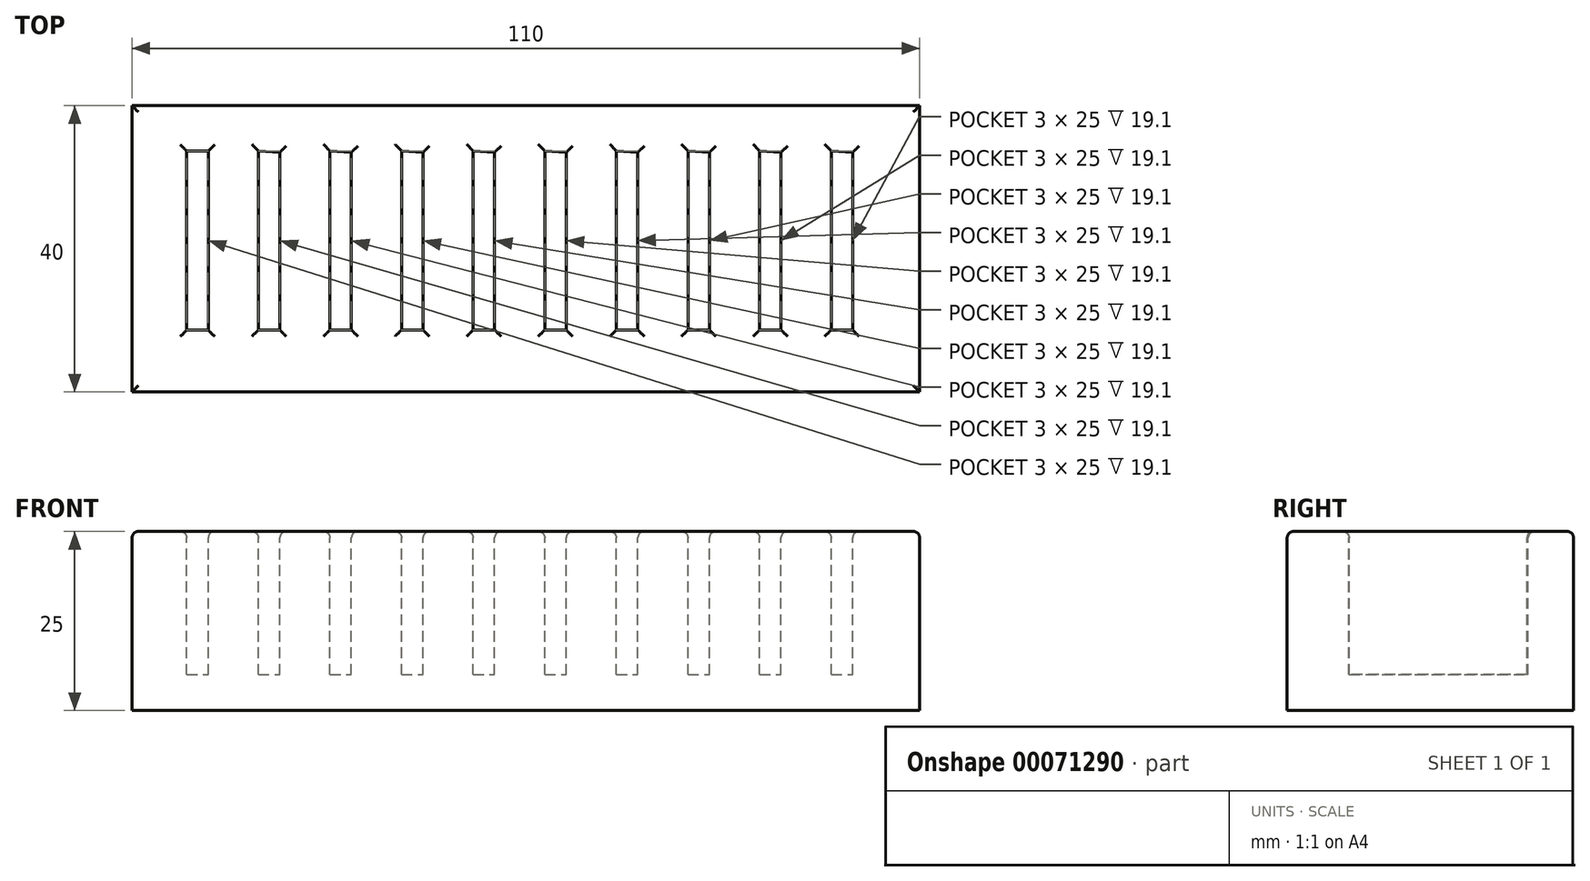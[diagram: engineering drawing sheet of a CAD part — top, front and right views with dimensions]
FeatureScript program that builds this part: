
annotation { "Feature Type Name" : "Feature", "Feature Type Description" : "" }
export const myFeature = defineFeature(function(context is Context, id is Id, definition is map)
    precondition{}
    {
        {
            var Q0;
            Q0=qCreatedBy(makeId("Top.planeOp"),FACE);
            var sketch = newSketch(context, id + "F0", { "sketchPlane" : qUnion([Q0])});
            skLineSegment(sketch, "E0.bottom", {"start": v(-54.52, 23.52) * mm, "end": v(55.48, 23.52) * mm});
            skLineSegment(sketch, "E0.top", {"start": v(-54.52, -16.48) * mm, "end": v(55.48, -16.48) * mm});
            skLineSegment(sketch, "E0.left", {"start": v(-54.52, 23.52) * mm, "end": v(-54.52, -16.48) * mm});
            skLineSegment(sketch, "E0.right", {"start": v(55.48, 23.52) * mm, "end": v(55.48, -16.48) * mm});
            skSolve(sketch);
        }
        {
            var Q0;
            Q0=makeQuery(id+"F0.imprint","IMPRINT",FACE,{"disambiguationData":[TD([[makeQuery(id+"F0.imprint","IMPRINT",EDGE,{"derivedFrom":sQuery(id+"F0.wireOp",EDGE,"E0.bottom")}),-1.0]])]});
            extrude(context, id + "F1", {"entities" : qUnion([Q0]), "depth" : 25 * mm});
        }
        {
            var Q0;
            Q0=makeQuery(id+"F1.opExtrude","CAP_FACE",FACE,{"disambiguationData":[OSD([sQuery(id+"F0.wireOp",EDGE,"E0.bottom"),sQuery(id+"F0.wireOp",EDGE,"E0.top"),sQuery(id+"F0.wireOp",EDGE,"E0.left"),sQuery(id+"F0.wireOp",EDGE,"E0.right")])],"isStart":false});
            var sketch = newSketch(context, id + "F2", { "sketchPlane" : qUnion([Q0])});
            skLineSegment(sketch, "E1.bottom", {"start": v(-46.88, -7.85) * mm, "end": v(-43.88, -7.85) * mm});
            skLineSegment(sketch, "E1.top", {"start": v(-46.88, 17.15) * mm, "end": v(-43.88, 17.15) * mm});
            skLineSegment(sketch, "E1.left", {"start": v(-46.88, -7.85) * mm, "end": v(-46.88, 17.15) * mm});
            skLineSegment(sketch, "E1.right", {"start": v(-43.88, -7.85) * mm, "end": v(-43.88, 17.15) * mm});
            skLineSegment(sketch, "E2", {"start": v(-43.88, -7.85) * mm, "end": v(-41.88, -7.83) * mm});
            skLineSegment(sketch, "E3.0", {"start": v(-36.88, -7.83) * mm, "end": v(-36.88, 17.17) * mm});
            skLineSegment(sketch, "E4", {"start": v(-36.88, -7.83) * mm, "end": v(-33.88, -7.83) * mm});
            skLineSegment(sketch, "E5", {"start": v(-33.88, 17.02) * mm, "end": v(-36.88, 17.17) * mm});
            skLineSegment(sketch, "E6", {"start": v(-33.88, 17.02) * mm, "end": v(-33.88, -7.83) * mm});
            skLineSegment(sketch, "E7.0", {"start": v(-26.88, -7.83) * mm, "end": v(-26.88, 17.17) * mm});
            skLineSegment(sketch, "E8.0", {"start": v(-16.88, -7.83) * mm, "end": v(-16.88, 17.17) * mm});
            skLineSegment(sketch, "E9.0", {"start": v(-6.88, -7.83) * mm, "end": v(-6.88, 17.17) * mm});
            skLineSegment(sketch, "E10.0", {"start": v(3.12, -7.83) * mm, "end": v(3.12, 17.17) * mm});
            skLineSegment(sketch, "E11.0", {"start": v(13.12, -7.83) * mm, "end": v(13.12, 17.17) * mm});
            skLineSegment(sketch, "E12.0", {"start": v(23.12, -7.83) * mm, "end": v(23.12, 17.17) * mm});
            skLineSegment(sketch, "E13.0", {"start": v(33.12, -7.83) * mm, "end": v(33.12, 17.17) * mm});
            skLineSegment(sketch, "E14.0", {"start": v(43.12, -7.83) * mm, "end": v(43.12, 17.17) * mm});
            skLineSegment(sketch, "E15.0", {"start": v(-23.88, 17.02) * mm, "end": v(-23.88, -7.83) * mm});
            skLineSegment(sketch, "E16.0", {"start": v(-13.88, 17.02) * mm, "end": v(-13.88, -7.83) * mm});
            skLineSegment(sketch, "E17.0", {"start": v(-3.88, 17.02) * mm, "end": v(-3.88, -7.83) * mm});
            skLineSegment(sketch, "E18.0", {"start": v(6.12, 17.02) * mm, "end": v(6.12, -7.83) * mm});
            skLineSegment(sketch, "E19.0", {"start": v(16.12, 17.02) * mm, "end": v(16.12, -7.83) * mm});
            skLineSegment(sketch, "E20.0", {"start": v(26.12, 17.02) * mm, "end": v(26.12, -7.83) * mm});
            skLineSegment(sketch, "E21.0", {"start": v(36.12, 17.02) * mm, "end": v(36.12, -7.83) * mm});
            skLineSegment(sketch, "E22.0", {"start": v(46.12, 17.02) * mm, "end": v(46.12, -7.83) * mm});
            skLineSegment(sketch, "E23", {"start": v(-26.88, 17.17) * mm, "end": v(-23.88, 17.02) * mm});
            skLineSegment(sketch, "E24", {"start": v(-26.88, -7.83) * mm, "end": v(-23.88, -7.83) * mm});
            skLineSegment(sketch, "E25", {"start": v(-16.88, 17.17) * mm, "end": v(-13.88, 17.02) * mm});
            skLineSegment(sketch, "E26", {"start": v(-16.88, -7.83) * mm, "end": v(-13.88, -7.83) * mm});
            skLineSegment(sketch, "E27", {"start": v(-6.88, -7.83) * mm, "end": v(-3.88, -7.83) * mm});
            skLineSegment(sketch, "E28", {"start": v(3.12, -7.83) * mm, "end": v(6.12, -7.83) * mm});
            skLineSegment(sketch, "E29", {"start": v(-6.88, 17.17) * mm, "end": v(-3.88, 17.02) * mm});
            skLineSegment(sketch, "E30", {"start": v(3.12, 17.17) * mm, "end": v(6.12, 17.02) * mm});
            skLineSegment(sketch, "E31", {"start": v(13.12, 17.17) * mm, "end": v(16.12, 17.02) * mm});
            skLineSegment(sketch, "E32", {"start": v(23.12, 17.17) * mm, "end": v(26.12, 17.02) * mm});
            skLineSegment(sketch, "E33", {"start": v(13.12, -7.83) * mm, "end": v(16.12, -7.83) * mm});
            skLineSegment(sketch, "E34", {"start": v(23.12, -7.83) * mm, "end": v(26.12, -7.83) * mm});
            skLineSegment(sketch, "E35", {"start": v(33.12, 17.17) * mm, "end": v(36.12, 17.02) * mm});
            skLineSegment(sketch, "E36", {"start": v(33.12, -7.83) * mm, "end": v(36.12, -7.83) * mm});
            skLineSegment(sketch, "E37", {"start": v(43.12, 17.17) * mm, "end": v(46.12, 17.02) * mm});
            skLineSegment(sketch, "E38", {"start": v(43.12, -7.83) * mm, "end": v(46.12, -7.83) * mm});
            skSolve(sketch);
        }
        {
            var Q0;
            Q0 = qSketchRegion(id + "F2", true);
            extrude(context, id + "F3", {"entities" : qUnion([Q0]), "operationType" : NewBodyOperationType.REMOVE, "oppositeDirection" : true, "depth" : 20 * mm});
        }
        {
            var Q0;
            Q0=makeQuery(id+"F1.opExtrude","CAP_FACE",FACE,{"disambiguationData":[OSD([sQuery(id+"F0.wireOp",EDGE,"E0.bottom"),sQuery(id+"F0.wireOp",EDGE,"E0.top"),sQuery(id+"F0.wireOp",EDGE,"E0.left"),sQuery(id+"F0.wireOp",EDGE,"E0.right")])],"isStart":false});
            fillet(context, id + "F4", {"entities" : qUnion([Q0]), "radius" : 0.9 * mm, "tangentPropagation" : true, "allowEdgeOverflow" : false});
        }
    });
